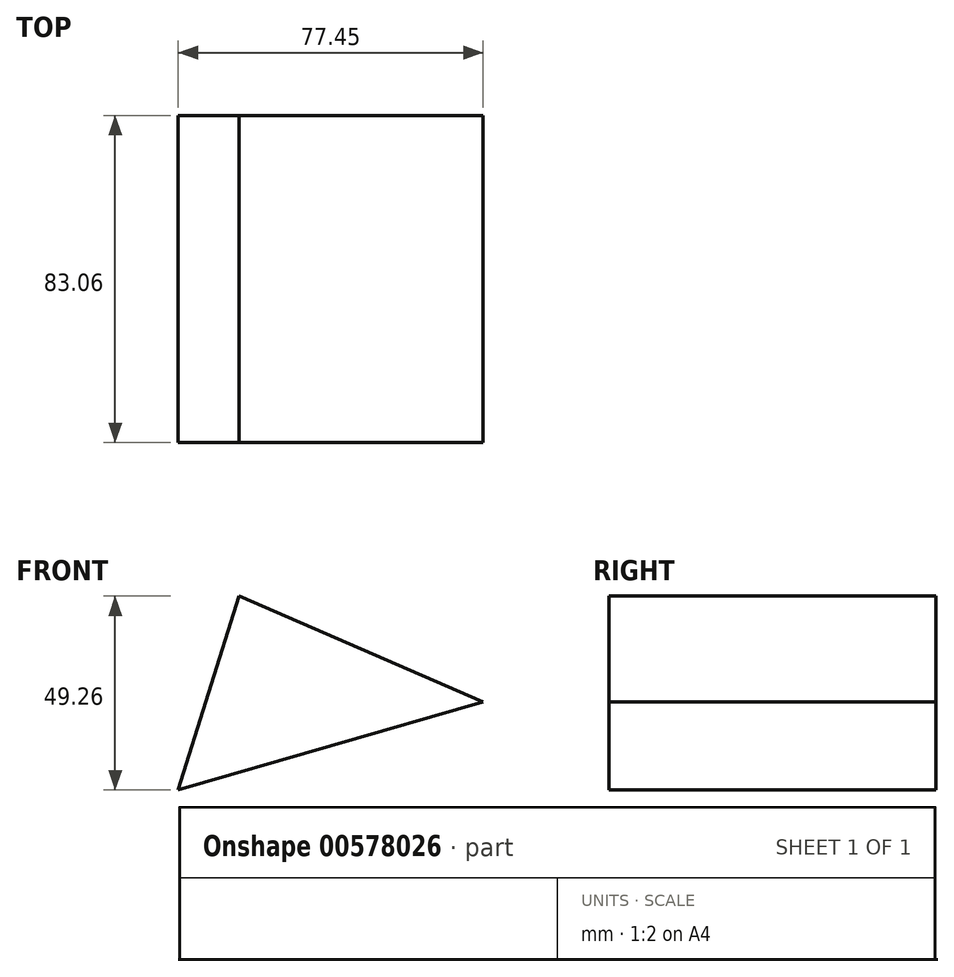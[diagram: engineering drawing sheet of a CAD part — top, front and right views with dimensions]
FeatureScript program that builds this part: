
annotation { "Feature Type Name" : "Feature", "Feature Type Description" : "" }
export const myFeature = defineFeature(function(context is Context, id is Id, definition is map)
    precondition{}
    {
        {
            var Q0;
            Q0=qCreatedBy(makeId("Front.planeOp"),FACE);
            var sketch = newSketch(context, id + "F0", { "sketchPlane" : qUnion([Q0])});
            skLineSegment(sketch, "E0", {"start": v(-51.52, 36.31) * mm, "end": v(-67.01, -12.95) * mm});
            skLineSegment(sketch, "E1", {"start": v(-67.01, -12.95) * mm, "end": v(10.44, 9.41) * mm});
            skLineSegment(sketch, "E2", {"start": v(10.44, 9.41) * mm, "end": v(-51.52, 36.31) * mm});
            skSolve(sketch);
        }
        {
            var Q0;
            Q0 = qSketchRegion(id + "F0", true);
            var Q1;
            Q1=sQuery(id+"F0.wireOp",EDGE,"E2");
            var Q2;
            Q2=sQuery(id+"F0.wireOp",EDGE,"E0");
            var Q3;
            Q3=sQuery(id+"F0.wireOp",EDGE,"E1");
            extrude(context, id + "F1", {"entities" : qUnion([Q0]), "bodyType" : ToolBodyType.SURFACE, "surfaceEntities" : qUnion([Q1, Q2, Q3]), "depth" : 83.06 * mm, "offsetDistance" : 25.4 * mm});
        }
    });
